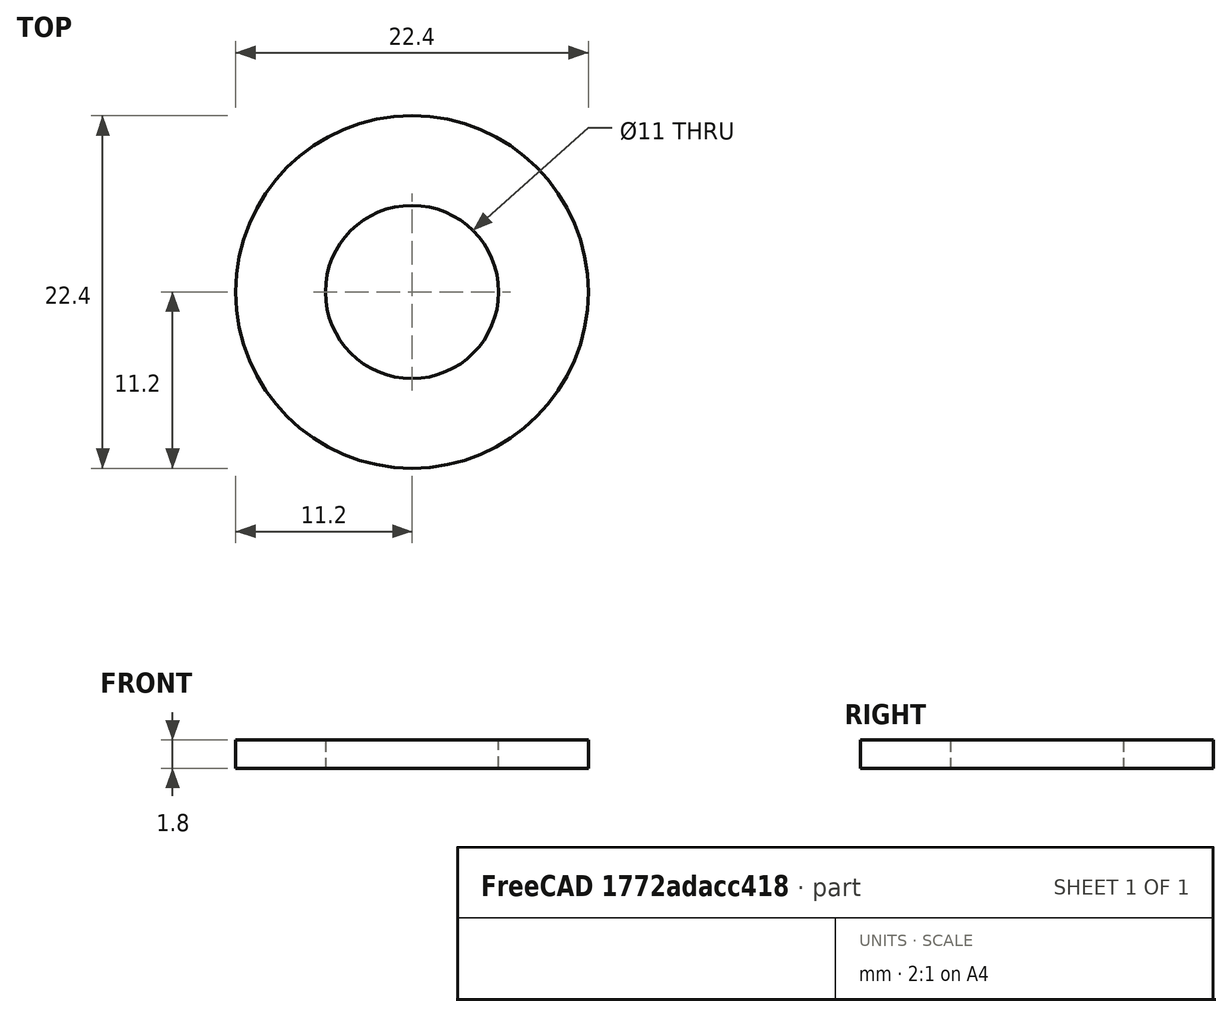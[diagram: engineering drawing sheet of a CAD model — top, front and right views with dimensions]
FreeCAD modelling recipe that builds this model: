
FCSTD DOCUMENT  (FreeCAD 0.20R29603 (Git))
Label: prekidac_2x_dno
License: All rights reserved
LicenseURL: http://en.wikipedia.org/wiki/All_rights_reserved
objects: Sketcher::SketchObject×1, PartDesign::Pad×1, PartDesign::Body×1
note: 4 computed .brp shape members not serialized (recipe doc carries the construction recipe); baked Part::Feature solids carry a one-line shape summary decoded from their .brp

FEATURE [Sketcher::SketchObject] Sketch
  FullyConstrained = true
  MapMode = 5
  Support = -> [XY_Plane]
  sketch-geometry (2):
    g0: Circle CenterX=0 CenterY=0 CenterZ=0 NormalX=0 NormalY=0 NormalZ=1 AngleXU=0 Radius=11.2
    g1: Circle CenterX=0 CenterY=0 CenterZ=0 NormalX=0 NormalY=0 NormalZ=1 AngleXU=0 Radius=5.5
  constraints (4):
    c: Coincident(g0,g-1)
    c: Diameter(g0) = 22.4
    c: Coincident(g1,g0)
    c: Diameter(g1) = 11
FEATURE [PartDesign::Pad] Pad
  Direction = (0,0,1)
  Length = 1.8
  Length2 = 10
  Profile = -> Sketch
  ReferenceAxis = -> Sketch [N_Axis]
  Type = 0
FEATURE [PartDesign::Body] Body
  Group = -> [Sketch,Pad]
  Origin = -> Origin
  Tip = -> Pad
